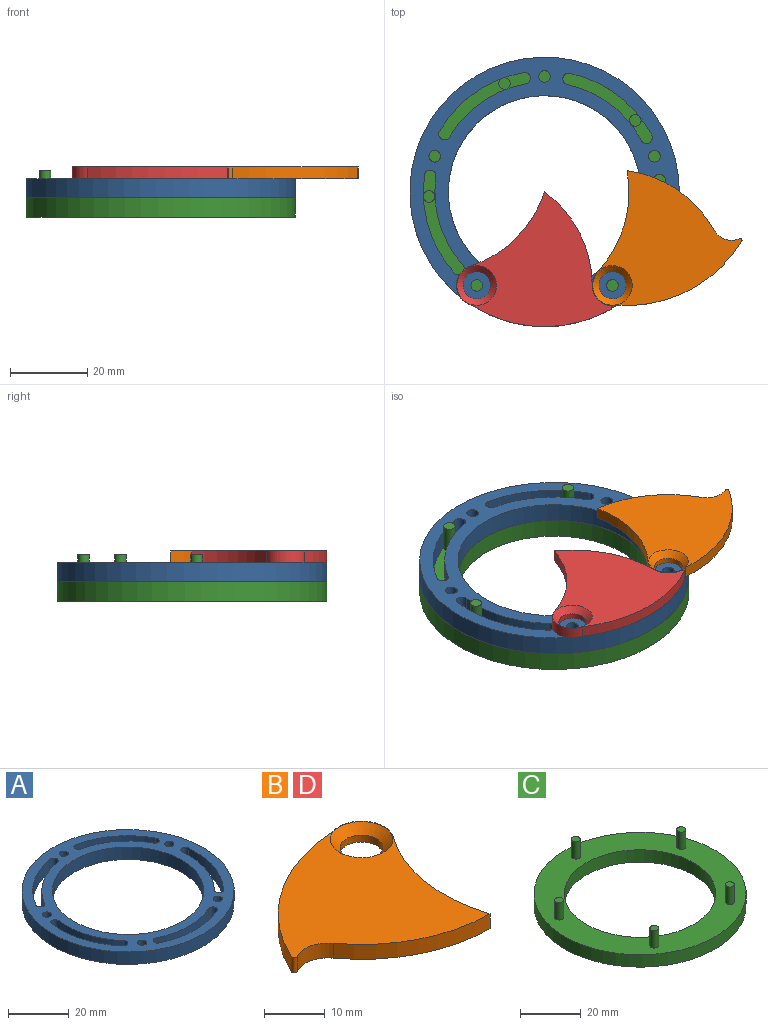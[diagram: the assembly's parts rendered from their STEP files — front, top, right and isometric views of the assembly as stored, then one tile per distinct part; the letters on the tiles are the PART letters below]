
ASSEMBLY  parts=4 mates=4
PART A: 29 faces, bbox 70x70x5 mm
  f0: cylinder r=1.5mm len=5mm, axis (0,0,-1), area 23.6mm2, adj f1,f26,f27,f28
  f1: cylinder r=28.5mm len=23.04mm, axis (0,0,-1), area 124.4mm2, adj f0,f2,f27,f28
  f2: cylinder r=1.5mm len=5mm, axis (0,0,-1), area 23.6mm2, adj f1,f26,f27,f28
  f3: cylinder r=1.5mm len=5mm, axis (0,0,-1), area 23.6mm2, adj f4,f15,f27,f28
  f4: cylinder r=28.5mm len=24.09mm, axis (0,0,-1), area 124.4mm2, adj f3,f5,f27,f28
  f5: cylinder r=1.5mm len=5mm, axis (0,0,-1), area 23.6mm2, adj f4,f15,f27,f28
  f6: cylinder r=1.5mm len=5mm, axis (0,0,-1), area 23.6mm2, adj f7,f16,f27,f28
  f7: cylinder r=28.5mm len=22.78mm, axis (0,0,-1), area 124.4mm2, adj f6,f8,f27,f28
  f8: cylinder r=1.5mm len=5mm, axis (0,0,-1), area 23.6mm2, adj f7,f16,f27,f28
  f9: cylinder r=1.5mm len=5mm, axis (0,0,-1), area 23.6mm2, adj f10,f17,f27,f28
  f10: cylinder r=28.5mm len=19.24mm, axis (0,0,-1), area 124.4mm2, adj f9,f11,f27,f28
  f11: cylinder r=1.5mm len=5mm, axis (0,0,-1), area 23.6mm2, adj f10,f17,f27,f28
  f12: cylinder r=31.5mm len=21.81mm, axis (0,0,-1), area 137.4mm2, adj f13,f25,f27,f28
  f13: cylinder r=1.5mm len=5mm, axis (0,0,-1), area 23.6mm2, adj f12,f14,f27,f28
  f14: cylinder r=28.5mm len=19.73mm, axis (0,0,-1), area 124.4mm2, adj f13,f25,f27,f28
  f15: cylinder r=31.5mm len=26.62mm, axis (0,0,-1), area 137.4mm2, adj f3,f5,f27,f28
  f16: cylinder r=31.5mm len=25.17mm, axis (0,0,-1), area 137.4mm2, adj f6,f8,f27,f28
  f17: cylinder r=31.5mm len=21.26mm, axis (0,0,-1), area 137.4mm2, adj f9,f11,f27,f28
  f18: cylinder r=35mm len=70mm, axis (0,0,-1), area 1099.6mm2, adj f27,f28
  f19: cylinder r=25mm len=50mm, axis (0,0,-1), area 785.4mm2, adj f27,f28
  f20: cylinder r=1.5mm len=5mm, axis (0,0,-1), area 47.1mm2, adj f27,f28
  f21: cylinder r=1.5mm len=5mm, axis (0,0,-1), area 47.1mm2, adj f27,f28
  f22: cylinder r=1.5mm len=5mm, axis (0,0,-1), area 47.1mm2, adj f27,f28
  f23: cylinder r=1.5mm len=5mm, axis (0,0,-1), area 47.1mm2, adj f27,f28
  f24: cylinder r=1.5mm len=5mm, axis (0,0,-1), area 47.1mm2, adj f27,f28
  f25: cylinder r=1.5mm len=5mm, axis (0,0,-1), area 23.6mm2, adj f12,f14,f27,f28
  f26: cylinder r=31.5mm len=25.46mm, axis (0,0,-1), area 137.4mm2, adj f0,f2,f27,f28
  f27: plane 70x70mm, normal (0,0,1), area 1421.6mm2, adj f0,f1,f2,f3,f4,f5,f6,f7
  f28: plane 70x70mm, normal (0,0,-1), area 1421.6mm2, adj f0,f1,f2,f3,f4,f5,f6,f7
PART B: 15 faces, bbox 37.2x35.3x3 mm
  f0: plane 37.18x35.27mm, normal (0,0,-1), area 564.3mm2, adj f1,f2,f3,f4,f5,f6,f8,f9
  f1: cylinder r=5.27mm len=8.36mm, axis (0,0,-1), area 40.2mm2, adj f0,f2,f6,f7
  f2: cylinder r=35mm len=30.08mm, axis (0,0,-1), area 114.8mm2, adj f0,f1,f7,f8
  f3: cylinder r=5.27mm len=6.89mm, axis (0,0,-1), area 23.2mm2, adj f0,f4,f7,f8
  f4: cylinder r=30mm len=24.27mm, axis (0,0,-1), area 84.8mm2, adj f0,f3,f6,f7
  f5: cylinder r=3.55mm len=7.1mm, axis (0,0,-1), area 31.2mm2, adj f0,f14
  f6: cylinder r=30mm len=26.9mm, axis (0,0,-1), area 84.8mm2, adj f0,f1,f4,f7
  f7: plane 37.18x35.27mm, normal (0,0,1), area 686.4mm2, adj f1,f2,f3,f4,f6,f8,f14
  f8: cylinder r=0.5mm len=3mm, axis (0,0,1), area 3.8mm2, adj f0,f2,f3,f7
  f9: plane 17.02x5.13mm, normal (0.29,0.96,0), area 35.5mm2, adj f0,f10,f12,f13
  f10: cylinder r=3.55mm len=6.95mm, axis (0,0,-1), area 22.3mm2, adj f0,f9,f11,f13
  f11: plane 17.02x5.13mm, normal (-0.29,-0.96,0), area 35.5mm2, adj f0,f10,f12,f13
  f12: cylinder r=3.55mm len=6.95mm, axis (0,0,-1), area 22.3mm2, adj f0,f9,f11,f13
  f13: plane 24.12x12.23mm, normal (0,0,-1), area 165.8mm2, adj f9,f10,f11,f12
  f14: cone r=3.55mm half-angle=45deg, axis (0,0,1), area 61.8mm2, adj f5,f7
PART C: 14 faces, bbox 70x70x12 mm
  f0: cylinder r=25mm len=50mm, axis (0,0,-1), area 785.4mm2, adj f2,f3
  f1: cylinder r=35mm len=70mm, axis (0,0,-1), area 1099.6mm2, adj f2,f3
  f2: plane 70x70mm, normal (0,0,1), area 1849.6mm2, adj f0,f1,f4,f6,f8,f10,f12
  f3: plane 70x70mm, normal (0,0,-1), area 1885mm2, adj f0,f1
  f4: cylinder r=1.5mm len=7mm, axis (0,0,-1), area 66mm2, adj f2,f5
  f5: plane 3x3mm, normal (0,0,1), area 7.1mm2, adj f4
  f6: cylinder r=1.5mm len=7mm, axis (0,0,-1), area 66mm2, adj f2,f7
  f7: plane 3x3mm, normal (0,0,1), area 7.1mm2, adj f6
  f8: cylinder r=1.5mm len=7mm, axis (0,0,-1), area 66mm2, adj f2,f9
  f9: plane 3x3mm, normal (0,0,1), area 7.1mm2, adj f8
  f10: cylinder r=1.5mm len=7mm, axis (0,0,-1), area 66mm2, adj f2,f11
  f11: plane 3x3mm, normal (0,0,1), area 7.1mm2, adj f10
  f12: cylinder r=1.5mm len=7mm, axis (0,0,-1), area 66mm2, adj f2,f13
  f13: plane 3x3mm, normal (0,0,1), area 7.1mm2, adj f12
PART D: same geometry as B
PLACE A at identity fixed
PLACE B rot(axis=(0,0,1),172.8deg) t=(21.41,5.49,5)mm
PLACE C rot(axis=(0,0,1),92.3deg) t=(0,0,-5)mm
PLACE D rot(axis=(0,0,1),144deg) t=(-0.02,0.01,5)mm
MATE pin_slot B.f12 <-> C.f8  axis (0,0,-1) through (42.37,-15.97,7)mm
MATE revolute A.f22 <-> D.f5  axis (0,0,1) through (-17.63,-24.27,5)mm
MATE revolute A.f23 <-> B.f5  axis (0,0,1) through (17.63,-24.27,5)mm
MATE revolute C.f1 <-> A.f19  axis (0,0,1) through (0,0,0)mm
